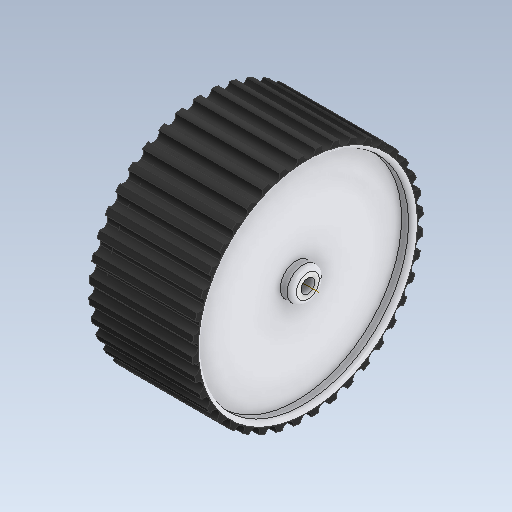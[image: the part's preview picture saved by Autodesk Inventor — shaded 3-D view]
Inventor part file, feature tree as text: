
AUTODESK INVENTOR PART (.ipt)
format: ipt  version: 2020 (Build 240168000, 168)  size: 672,768 bytes
history: native  units: in
note: dims shown in document units (in); Inventor stores cm internally (conversion verified against a paired STEP export)
features: sketch x6, extrude x5, fillet x5, hole x1, other x1
ambient origin geometry x8: Origin, YZ Plane, XZ Plane, XY Plane, X Axis, Y Axis, Z Axis, Center Point
bodies: Solid4 (feature_tree)
feature tree (18):
  extrude  "Extrusion4"  Depth=3.937in
  extrude  "Extrusion5"  Depth=3.7402in
  hole  "Hole2"  [1 undecoded]
  extrude  "Extrusion6"  Depth=3.1496in TaperAngle=360.0deg
  extrude  "Extrusion8"  Depth=0.552in
  extrude  "Extrusion9"  Depth=3.5923in
  fillet  "Fillet1"  Radius=0.1969in
  fillet  "Fillet2"  Radius=0.0787in
  fillet  "Fillet3"  Radius=0.0787in
  fillet  "Fillet4"  Radius=0.0787in
  fillet  "Fillet5"  Radius=0.0787in
  other  "Work Axis1"
  sketch  "Sketch7"  dims[d17=3.7402in d18=3.937in]
  sketch  "Sketch8"  dims[d19=1.7717in d20=0.0in d21=3.7402in]
  sketch  "Sketch9"  dims[d22=1.5748in d23=0.0in]
  sketch  "Sketch10"  dims[d24=0.2362in d25=0.2362in d26=0.1575in d27=0.0787in d28=90.0deg d29=0.315in d30=0.8108in d31=15.748in d33=360.0deg]
  sketch  "Sketch13"  dims[d35=1.7717in d36=0.0in d48=3.1496in d50=360.0deg]
  sketch  "Sketch14"  dims[d52=0.5906in d53=0.0in d54=0.552in d55=3.5923in d56=0.1969in d57=0.0in d58=0.0787in d59=0.0787in d60=0.0787in d61=0.0787in d62=0.0787in d32=0.8108in d34=0.0295in d37=0.0197in d38=0.0344in]
note: 1 required parameter value undecoded (feature->parameter linkage not recoverable at this tier; creation-order binding heuristic only, values carry confidence <= 0.55)
